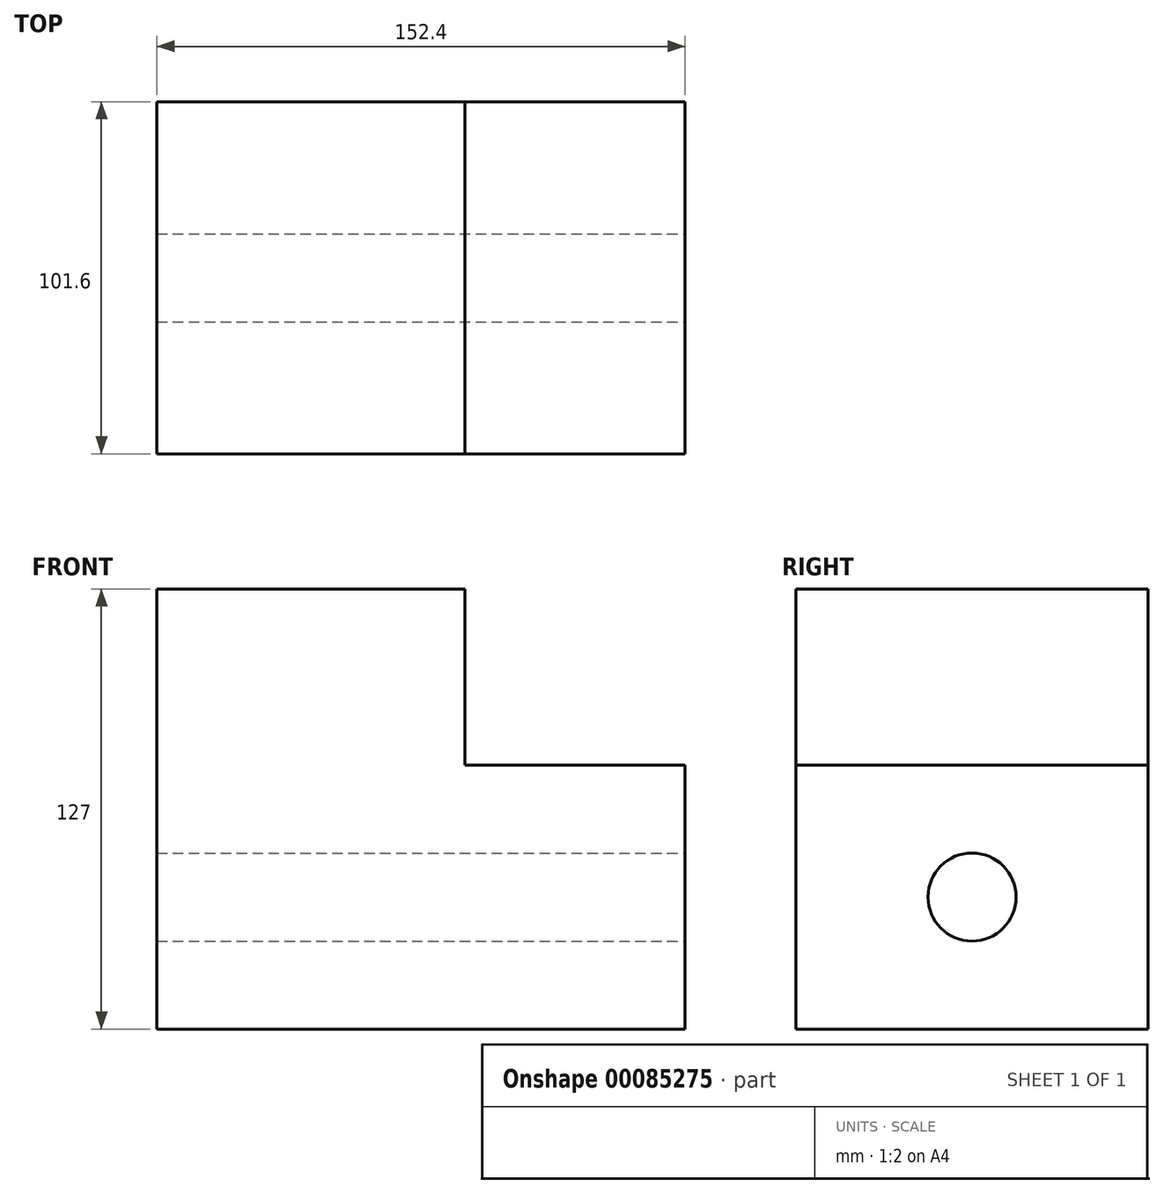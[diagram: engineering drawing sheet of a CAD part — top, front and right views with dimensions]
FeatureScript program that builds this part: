
annotation { "Feature Type Name" : "Feature", "Feature Type Description" : "" }
export const myFeature = defineFeature(function(context is Context, id is Id, definition is map)
    precondition{}
    {
        {
            var Q0;
            Q0=qCreatedBy(makeId("Top.planeOp"),FACE);
            var sketch = newSketch(context, id + "F0", { "sketchPlane" : qUnion([Q0])});
            skLineSegment(sketch, "E0.bottom", {"start": v(-76.63, 64.42) * mm, "end": v(75.77, 64.42) * mm});
            skLineSegment(sketch, "E0.top", {"start": v(-76.63, -37.18) * mm, "end": v(75.77, -37.18) * mm});
            skLineSegment(sketch, "E0.left", {"start": v(-76.63, 64.42) * mm, "end": v(-76.63, -37.18) * mm});
            skLineSegment(sketch, "E0.right", {"start": v(75.77, 64.42) * mm, "end": v(75.77, -37.18) * mm});
            skSolve(sketch);
        }
        {
            var Q0;
            Q0=makeQuery(id+"F0.imprint","IMPRINT",FACE,{"disambiguationData":[TD([[makeQuery(id+"F0.imprint","IMPRINT",EDGE,{"derivedFrom":sQuery(id+"F0.wireOp",EDGE,"E0.bottom")}),-1.0]])]});
            extrude(context, id + "F1", {"entities" : qUnion([Q0]), "depth" : 76.2 * mm});
        }
        {
            var Q0;
            Q0=makeQuery(id+"F1.opExtrude","CAP_FACE",FACE,{"disambiguationData":[OSD([sQuery(id+"F0.wireOp",EDGE,"E0.bottom"),sQuery(id+"F0.wireOp",EDGE,"E0.top"),sQuery(id+"F0.wireOp",EDGE,"E0.left"),sQuery(id+"F0.wireOp",EDGE,"E0.right")])],"isStart":false});
            var sketch = newSketch(context, id + "F2", { "sketchPlane" : qUnion([Q0])});
            skLineSegment(sketch, "E1.bottom", {"start": v(-76.63, 64.42) * mm, "end": v(12.27, 64.42) * mm});
            skLineSegment(sketch, "E1.top", {"start": v(-76.63, -37.18) * mm, "end": v(12.27, -37.18) * mm});
            skLineSegment(sketch, "E1.left", {"start": v(-76.63, 64.42) * mm, "end": v(-76.63, -37.18) * mm});
            skLineSegment(sketch, "E1.right", {"start": v(12.27, 64.42) * mm, "end": v(12.27, -37.18) * mm});
            skSolve(sketch);
        }
        {
            var Q0;
            Q0=makeQuery(id+"F2.imprint","IMPRINT",FACE,{"disambiguationData":[TD([[makeQuery(id+"F2.imprint","IMPRINT",EDGE,{"derivedFrom":sQuery(id+"F2.wireOp",EDGE,"E1.bottom")}),-1.0]])]});
            extrude(context, id + "F3", {"entities" : qUnion([Q0]), "operationType" : NewBodyOperationType.ADD, "depth" : 50.8 * mm});
        }
        {
            var Q0;
            Q0=makeQuery(id+"F1.opExtrude","SWEPT_FACE",FACE,{"disambiguationData":[OSD([sQuery(id+"F0.wireOp",EDGE,"E0.right")])]});
            var sketch = newSketch(context, id + "F4", { "sketchPlane" : qUnion([Q0])});
            skLineSegment(sketch, "E2.bottom", {"start": v(-37.18, 0) * mm, "end": v(13.62, 0) * mm});
            skLineSegment(sketch, "E2.top", {"start": v(-37.18, 38.1) * mm, "end": v(13.62, 38.1) * mm});
            skLineSegment(sketch, "E2.left", {"start": v(-37.18, 0) * mm, "end": v(-37.18, 38.1) * mm});
            skLineSegment(sketch, "E2.right", {"start": v(13.62, 0) * mm, "end": v(13.62, 38.1) * mm});
            skSolve(sketch);
        }
        {
            var Q0;
            Q0=sQuery(id+"F4.wireOp",VERTEX,"E2.top.end");
            var Q1;
            Q1=makeQuery(id+"F1.opExtrude","SWEPT_BODY",BODY,{"disambiguationData":[OSD([sQuery(id+"F0.wireOp",EDGE,"E0.bottom"),sQuery(id+"F0.wireOp",EDGE,"E0.top"),sQuery(id+"F0.wireOp",EDGE,"E0.left"),sQuery(id+"F0.wireOp",EDGE,"E0.right")])]});
            hole(context, id + "F5", {"style" : HoleStyle.SIMPLE, "endStyle" : HoleEndStyle.THROUGH, "holeDiameter" : 25.4 * mm, "startFromSketch" : true, "locations" : qUnion([Q0]), "scope" : qUnion([Q1]), "isTappedThrough" : true});
        }
    });
